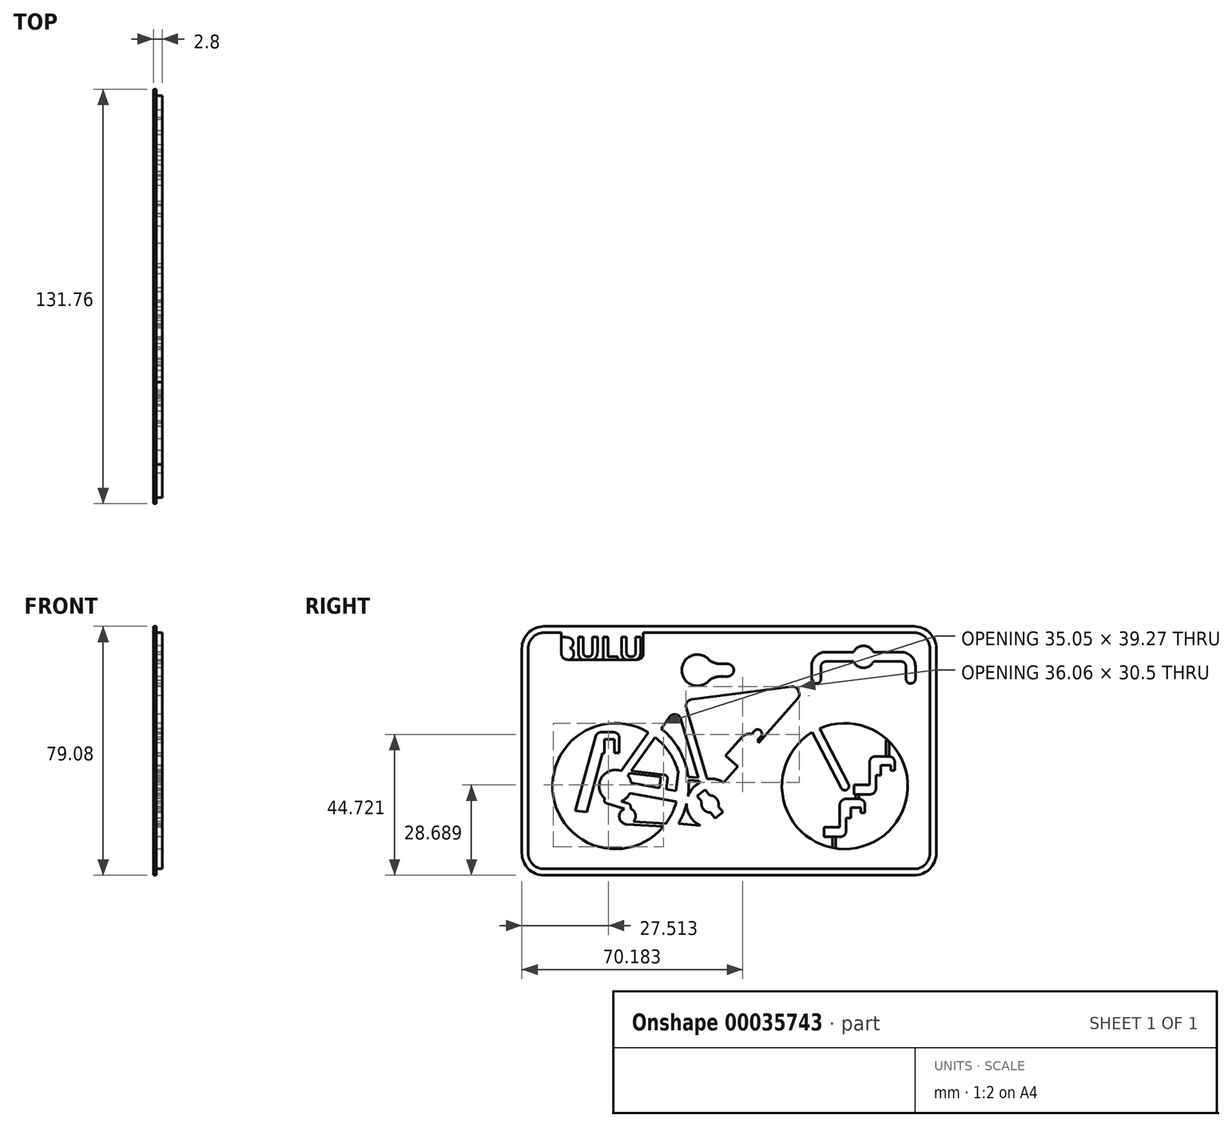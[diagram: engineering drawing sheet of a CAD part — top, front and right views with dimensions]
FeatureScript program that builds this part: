
annotation { "Feature Type Name" : "Feature", "Feature Type Description" : "" }
export const myFeature = defineFeature(function(context is Context, id is Id, definition is map)
    precondition{}
    {
        {
            assignVariable(context, id + "F0", {"name" : "H", "anyValue" : 2.8});
        }
        {
            var Q0;
            Q0=qCreatedBy(makeId("Right.planeOp"),FACE);
            var sketch = newSketch(context, id + "F1", { "sketchPlane" : qUnion([Q0])});
            skArc(sketch, "E0", {"start": v(-24.13, -6.05) * mm, "mid": v(-23.9, -3.4) * mm, "end": v(-23.98, -0.75) * mm});
            skLineSegment(sketch, "E1.0.left", {"start": v(-28.58, 25.85) * mm, "end": v(-32.78, 40.06) * mm});
            skLineSegment(sketch, "E1.0.right", {"start": v(-26.16, 27.08) * mm, "end": v(-30, 40.23) * mm});
            skLineSegment(sketch, "E2.0.startCap", {"start": v(-28.4, 25.23) * mm, "end": v(-28.4, 25.23) * mm});
            skLineSegment(sketch, "E2.0.left", {"start": v(-24.73, 22.24) * mm, "end": v(-18.03, -0.43) * mm});
            skLineSegment(sketch, "E2.0.right", {"start": v(-26.45, 18.66) * mm, "end": v(-20.9, -0.08) * mm});
            skLineSegment(sketch, "E2.1.endCap", {"start": v(-25.84, 25.99) * mm, "end": v(-25.84, 25.99) * mm});
            skLineSegment(sketch, "E2.1.left", {"start": v(-45.44, 2.11) * mm, "end": v(-36.77, 14.32) * mm});
            skLineSegment(sketch, "E2.2.startCap", {"start": v(-28.4, 25.23) * mm, "end": v(-28.4, 25.23) * mm});
            skLineSegment(sketch, "E2.2.endCap", {"start": v(12.78, 30.97) * mm, "end": v(12.78, 30.97) * mm});
            skLineSegment(sketch, "E2.2.left", {"start": v(-26.16, 27.08) * mm, "end": v(9.78, 31.72) * mm});
            skArc(sketch, "E2.3.endCap", {"start": v(14.25, 26) * mm, "mid": v(14.25, 25.99) * mm, "end": v(14.25, 25.98) * mm});
            skLineSegment(sketch, "E2.3.right", {"start": v(-10.81, -3.35) * mm, "end": v(12.38, 22.92) * mm});
            skLineSegment(sketch, "E2.4.left", {"start": v(10.82, 37.6) * mm, "end": v(12.78, 30.97) * mm});
            skLineSegment(sketch, "E2.4.right", {"start": v(8.04, 37.6) * mm, "end": v(9.78, 31.72) * mm});
            skLineSegment(sketch, "E2.5.startCap", {"start": v(10.22, 30.22) * mm, "end": v(10.22, 30.22) * mm});
            skLineSegment(sketch, "E2.5.left", {"start": v(12.78, 30.97) * mm, "end": v(16.41, 18.68) * mm});
            skLineSegment(sketch, "E2.5.right", {"start": v(11.03, 27.5) * mm, "end": v(11.17, 27) * mm});
            skArc(sketch, "E2.6.endCap", {"start": v(26.9, -2.1) * mm, "mid": v(26.33, -3.9) * mm, "end": v(24.53, -3.33) * mm});
            skLineSegment(sketch, "E2.6.left", {"start": v(17.7, 15.6) * mm, "end": v(26.9, -2.1) * mm});
            skLineSegment(sketch, "E2.6.right", {"start": v(15.34, 14.38) * mm, "end": v(24.53, -3.33) * mm});
            skArc(sketch, "E3", {"start": v(15.34, 14.38) * mm, "mid": v(34.93, -20.47) * mm, "end": v(17.7, 15.6) * mm});
            skArc(sketch, "E4", {"start": v(-45.44, 2.11) * mm, "mid": v(-51.68, -0.11) * mm, "end": v(-50.57, -6.64) * mm});
            skLineSegment(sketch, "E5.0.right", {"start": v(-42.59, -4.95) * mm, "end": v(-27.87, -7.72) * mm});
            skLineSegment(sketch, "E6.trimOffspring", {"start": v(-23.07, 24.79) * mm, "end": v(8.85, 28.9) * mm});
            skLineSegment(sketch, "E7.trimOffspring", {"start": v(-43.27, 0.57) * mm, "end": v(-42.74, 1.31) * mm});
            skArc(sketch, "E8.trimOffspring", {"start": v(-42.19, -1.68) * mm, "mid": v(-42.59, -0.49) * mm, "end": v(-43.27, 0.57) * mm});
            skArc(sketch, "E9.trimOffspring", {"start": v(-36.77, 14.32) * mm, "mid": v(-66.97, -5.92) * mm, "end": v(-31.92, -15.58) * mm});
            skArc(sketch, "E10.trimOffspring", {"start": v(-34.83, 17.05) * mm, "mid": v(-70.04, -7.66) * mm, "end": v(-27.76, -15.58) * mm});
            skLineSegment(sketch, "E11.trimOffspring", {"start": v(-32.66, 15.5) * mm, "end": v(-30, 19.25) * mm});
            skLineSegment(sketch, "E12.trimOffspring", {"start": v(-34.83, 17.05) * mm, "end": v(-28.58, 25.85) * mm});
            skLineSegment(sketch, "E13.trimOffspring", {"start": v(-12.8, -1.58) * mm, "end": v(-9.7, 1.94) * mm});
            skLineSegment(sketch, "E14.trimOffspring", {"start": v(12.38, 22.92) * mm, "end": v(14, 17.45) * mm});
            skArc(sketch, "E15.trimOffspring", {"start": v(14, 17.45) * mm, "mid": v(36.24, -23.54) * mm, "end": v(16.41, 18.68) * mm});
            skArc(sketch, "E16", {"start": v(-24.58, -8.33) * mm, "mid": v(-23.45, -12.4) * mm, "end": v(-20.3, -15.22) * mm});
            skLineSegment(sketch, "E17", {"start": v(-43.4, -10.23) * mm, "end": v(-43.4, -10.23) * mm});
            skArc(sketch, "E18.0.endCap", {"start": v(-50.06, -8.17) * mm, "mid": v(-50.7, -7.54) * mm, "end": v(-50.57, -6.64) * mm});
            skArc(sketch, "E18.1.startCap", {"start": v(-50.06, -8.17) * mm, "mid": v(-50.7, -7.54) * mm, "end": v(-50.57, -6.64) * mm});
            skArc(sketch, "E18.1.endCap", {"start": v(-43.1, -8.28) * mm, "mid": v(-42.59, -8.64) * mm, "end": v(-42.4, -9.23) * mm});
            skLineSegment(sketch, "E18.1.right", {"start": v(-50.06, -8.17) * mm, "end": v(-44.44, -9.95) * mm});
            skLineSegment(sketch, "E18.2.left", {"start": v(-42.4, -9.23) * mm, "end": v(-42.4, -9.93) * mm});
            skArc(sketch, "E19.trimOffspring", {"start": v(-45.42, -7.54) * mm, "mid": v(-43.75, -6.52) * mm, "end": v(-42.59, -4.95) * mm});
            skLineSegment(sketch, "E20.trimOffspring", {"start": v(-45.42, -7.54) * mm, "end": v(-43.1, -8.28) * mm});
            skPoint(sketch, "E21.visualSharp", {"position": v(-25.4, 24.49) * mm});
            skArc(sketch, "E21.filletArc", {"start": v(-23.07, 24.79) * mm, "mid": v(-24.49, 23.9) * mm, "end": v(-24.73, 22.24) * mm});
            skPoint(sketch, "E22.visualSharp", {"position": v(-27.62, 22.6) * mm});
            skArc(sketch, "E22.filletArc", {"start": v(-26.45, 18.66) * mm, "mid": v(-28.04, 20.06) * mm, "end": v(-30, 19.25) * mm});
            skPoint(sketch, "E23.visualSharp", {"position": v(10.54, 29.13) * mm});
            skArc(sketch, "E23.filletArc", {"start": v(11.03, 27.5) * mm, "mid": v(10.2, 28.6) * mm, "end": v(8.85, 28.9) * mm});
            skPoint(sketch, "E24.visualSharp", {"position": v(11.49, 25.94) * mm});
            skArc(sketch, "E24.filletArc", {"start": v(10.75, 25.11) * mm, "mid": v(11.2, 26) * mm, "end": v(11.17, 27) * mm});
            skArc(sketch, "E25.trimOffspring", {"start": v(-20.43, -1.7) * mm, "mid": v(-22.71, -3.5) * mm, "end": v(-24.13, -6.05) * mm});
            skArc(sketch, "E26.0.endCap", {"start": v(-6.97, 12.85) * mm, "mid": v(-5.59, 13.74) * mm, "end": v(-3.94, 13.76) * mm});
            skLineSegment(sketch, "E26.0.left", {"start": v(-12.2, 6.92) * mm, "end": v(-6.97, 12.85) * mm});
            skLineSegment(sketch, "E27.trimOffspring", {"start": v(-1.72, 10.98) * mm, "end": v(10.75, 25.11) * mm});
            skLineSegment(sketch, "E28", {"start": v(-12.2, 6.92) * mm, "end": v(-8.33, 3.5) * mm});
            skLineSegment(sketch, "E29", {"start": v(-9.7, 1.94) * mm, "end": v(-8.33, 3.5) * mm});
            skArc(sketch, "E30.0.endCap", {"start": v(-3, 14.84) * mm, "mid": v(-1.11, 14.95) * mm, "end": v(-1, 13.07) * mm});
            skLineSegment(sketch, "E30.0.left", {"start": v(-3.94, 13.76) * mm, "end": v(-3, 14.84) * mm});
            skLineSegment(sketch, "E30.0.right", {"start": v(-1.94, 12) * mm, "end": v(-1, 13.07) * mm});
            skArc(sketch, "E31.trimOffspring", {"start": v(-1.94, 12) * mm, "mid": v(-1.79, 11.5) * mm, "end": v(-1.72, 10.98) * mm});
            skArc(sketch, "E32.0.endCap", {"start": v(-11.57, 36.12) * mm, "mid": v(-9.57, 34.12) * mm, "end": v(-11.57, 32.12) * mm});
            skLineSegment(sketch, "E32.0.left", {"start": v(-13.75, 36.12) * mm, "end": v(-11.57, 36.12) * mm});
            skLineSegment(sketch, "E32.0.right", {"start": v(-13.75, 32.12) * mm, "end": v(-11.57, 32.12) * mm});
            skPoint(sketch, "E33.visualSharp", {"position": v(-17.03, 36.12) * mm});
            skArc(sketch, "E33.filletArc", {"start": v(-17.4, 37.36) * mm, "mid": v(-15.68, 36.44) * mm, "end": v(-13.75, 36.12) * mm});
            skPoint(sketch, "E34.visualSharp", {"position": v(-17.03, 32.12) * mm});
            skArc(sketch, "E34.filletArc", {"start": v(-13.75, 32.12) * mm, "mid": v(-15.68, 31.8) * mm, "end": v(-17.4, 30.88) * mm});
            skLineSegment(sketch, "E35", {"start": v(-32.78, 40.06) * mm, "end": v(-32.78, 43.03) * mm});
            skLineSegment(sketch, "E36", {"start": v(-32.78, 43.03) * mm, "end": v(-30, 43.03) * mm});
            skLineSegment(sketch, "E37", {"start": v(-30, 43.03) * mm, "end": v(-30, 40.23) * mm});
            skLineSegment(sketch, "E38.rect.bottom", {"start": v(-22.8, 35.76) * mm, "end": v(-19.51, 35.76) * mm});
            skLineSegment(sketch, "E38.rect.top", {"start": v(-22.8, 32.47) * mm, "end": v(-19.51, 32.47) * mm});
            skLineSegment(sketch, "E38.rect.left", {"start": v(-22.8, 35.76) * mm, "end": v(-22.8, 32.47) * mm});
            skLineSegment(sketch, "E38.rect.right", {"start": v(-19.51, 35.76) * mm, "end": v(-19.51, 32.47) * mm});
            skPoint(sketch, "E38.rect.middle", {"position": v(-21.16, 34.12) * mm});
            skLineSegment(sketch, "E39", {"start": v(8.04, 37.6) * mm, "end": v(8.04, 40.4) * mm});
            skLineSegment(sketch, "E40", {"start": v(10.82, 37.6) * mm, "end": v(10.82, 40.4) * mm});
            skLineSegment(sketch, "E41", {"start": v(10.82, 40.4) * mm, "end": v(8.04, 40.4) * mm});
            skLineSegment(sketch, "E42.1.startCap", {"start": v(-20.7, -0.1) * mm, "end": v(-20.7, -0.1) * mm});
            skLineSegment(sketch, "E42.1.left", {"start": v(-20.6, -1.12) * mm, "end": v(-23.98, -0.75) * mm});
            skLineSegment(sketch, "E42.1.right", {"start": v(-20.9, -0.08) * mm, "end": v(-24.09, 0.27) * mm});
            skLineSegment(sketch, "E42.2.left", {"start": v(-41.45, -14.01) * mm, "end": v(-31.17, -14.62) * mm});
            skLineSegment(sketch, "E42.2.right", {"start": v(-43.68, -14.88) * mm, "end": v(-31.92, -15.58) * mm});
            skArc(sketch, "E42.3.right", {"start": v(-44.44, -9.95) * mm, "mid": v(-45.92, -12.84) * mm, "end": v(-43.4, -14.9) * mm});
            skArc(sketch, "E42.4.startCap", {"start": v(-17.41, -16.44) * mm, "mid": v(-17.42, -16.43) * mm, "end": v(-17.43, -16.43) * mm});
            skLineSegment(sketch, "E42.4.left", {"start": v(-17.43, -16.43) * mm, "end": v(-27.76, -15.58) * mm});
            skArc(sketch, "E42.5.right", {"start": v(-17.41, -16.44) * mm, "mid": v(-9.88, -12.02) * mm, "end": v(-10.81, -3.35) * mm});
            skArc(sketch, "E42.6.right", {"start": v(-12.8, -1.58) * mm, "mid": v(-15.32, -0.56) * mm, "end": v(-18.03, -0.43) * mm});
            skArc(sketch, "E43.trimOffspring", {"start": v(-24.09, 0.27) * mm, "mid": v(-26.9, 8.72) * mm, "end": v(-32.66, 15.5) * mm});
            skLineSegment(sketch, "E44.trimOffspring", {"start": v(-20.6, -1.12) * mm, "end": v(-20.43, -1.7) * mm});
            skLineSegment(sketch, "E45.trimOffspring", {"start": v(-42.17, 2.12) * mm, "end": v(-34.6, 12.78) * mm});
            skArc(sketch, "E46.trimOffspring", {"start": v(-41.45, -14.01) * mm, "mid": v(-40.88, -11.73) * mm, "end": v(-42.4, -9.93) * mm});
            skArc(sketch, "E47.trimOffspring", {"start": v(-31.17, -14.62) * mm, "mid": v(-29.19, -11.33) * mm, "end": v(-27.87, -7.72) * mm});
            skArc(sketch, "E48.trimOffspring", {"start": v(-27.16, -14.62) * mm, "mid": v(-25.64, -11.57) * mm, "end": v(-24.58, -8.33) * mm});
            skLineSegment(sketch, "E49.trimOffspring", {"start": v(-20.3, -15.22) * mm, "end": v(-27.16, -14.62) * mm});
            skPoint(sketch, "E42.2.endCap.center.orphan", {"position": v(-31.53, -15.1) * mm});
            skPoint(sketch, "E42.4.endCap.center.orphan", {"position": v(-27.45, -15.1) * mm});
            skArc(sketch, "E50.trimOffspring", {"start": v(-17.89, -15.9) * mm, "mid": v(-17.89, -15.9) * mm, "end": v(-17.89, -15.9) * mm});
            skLineSegment(sketch, "E51.rect.bottom", {"start": v(26.14, -12.83) * mm, "end": v(27.64, -12.83) * mm});
            skLineSegment(sketch, "E51.rect.top", {"start": v(26.14, -6.83) * mm, "end": v(30.34, -6.83) * mm});
            skLineSegment(sketch, "E51.rect.right", {"start": v(32.14, -11.23) * mm, "end": v(32.14, -8.62) * mm});
            skPoint(sketch, "E51.rect.middle", {"position": v(29.14, -9.83) * mm});
            skLineSegment(sketch, "E52.0.left", {"start": v(30.84, -9.63) * mm, "end": v(30.84, -11.23) * mm});
            skLineSegment(sketch, "E52.0.right", {"start": v(27.64, -9.63) * mm, "end": v(27.64, -12.83) * mm});
            skPoint(sketch, "E52.0.endCap.center.orphan", {"position": v(29.14, -12.83) * mm});
            skLineSegment(sketch, "E53.rect.top", {"start": v(-51.76, 14.4) * mm, "end": v(-47.77, 14.4) * mm});
            skLineSegment(sketch, "E54.0.left", {"start": v(-47.56, 12.2) * mm, "end": v(-47.56, 7.8) * mm});
            skLineSegment(sketch, "E53.rect.bottom", {"start": v(-51.4, 7.66) * mm, "end": v(-50.76, 7.66) * mm});
            skLineSegment(sketch, "E54.0.right", {"start": v(-50.76, 12.2) * mm, "end": v(-50.76, 7.66) * mm});
            skPoint(sketch, "E53.rect.middle", {"position": v(-48.46, 11.03) * mm});
            skLineSegment(sketch, "E55.bottom", {"start": v(26.14, -6.83) * mm, "end": v(25.93, -6.83) * mm});
            skLineSegment(sketch, "E55.left", {"start": v(26.14, -12.83) * mm, "end": v(26.14, -17.03) * mm});
            skLineSegment(sketch, "E55.right", {"start": v(24.14, -8.62) * mm, "end": v(24.14, -15.83) * mm});
            skLineSegment(sketch, "E56.top", {"start": v(24.14, -15.83) * mm, "end": v(19.14, -15.83) * mm});
            skLineSegment(sketch, "E56.right", {"start": v(19.14, -18.83) * mm, "end": v(19.14, -15.83) * mm});
            skLineSegment(sketch, "E57", {"start": v(19.14, -18.83) * mm, "end": v(24.34, -18.83) * mm});
            skPoint(sketch, "E58.visualSharp", {"position": v(26.14, -18.83) * mm});
            skArc(sketch, "E58.filletArc", {"start": v(24.34, -18.83) * mm, "mid": v(25.6, -18.3) * mm, "end": v(26.14, -17.03) * mm});
            skPoint(sketch, "E59.visualSharp", {"position": v(32.14, -6.83) * mm});
            skArc(sketch, "E59.filletArc", {"start": v(32.14, -8.62) * mm, "mid": v(31.6, -7.35) * mm, "end": v(30.34, -6.83) * mm});
            skPoint(sketch, "E60.visualSharp", {"position": v(24.14, -6.83) * mm});
            skArc(sketch, "E60.filletArc", {"start": v(25.93, -6.83) * mm, "mid": v(24.66, -7.35) * mm, "end": v(24.14, -8.62) * mm});
            skPoint(sketch, "E61.visualSharp", {"position": v(24.14, -15.83) * mm});
            skLineSegment(sketch, "E62", {"start": v(27.64, -9.63) * mm, "end": v(30.84, -9.63) * mm});
            skLineSegment(sketch, "E63", {"start": v(-51.4, 7.66) * mm, "end": v(-56.37, -10.97) * mm});
            skLineSegment(sketch, "E64", {"start": v(-60.02, -10.55) * mm, "end": v(-53.5, 13.08) * mm});
            skPoint(sketch, "E65.visualSharp", {"position": v(-53.13, 14.4) * mm});
            skArc(sketch, "E65.filletArc", {"start": v(-51.76, 14.4) * mm, "mid": v(-52.85, 14.03) * mm, "end": v(-53.5, 13.08) * mm});
            skPoint(sketch, "E66.visualSharp", {"position": v(-45.51, 14.4) * mm});
            skArc(sketch, "E66.filletArc", {"start": v(-45.97, 12.6) * mm, "mid": v(-46.5, 13.87) * mm, "end": v(-47.77, 14.4) * mm});
            skLineSegment(sketch, "E67", {"start": v(-50.76, 12.2) * mm, "end": v(-47.56, 12.2) * mm});
            skLineSegment(sketch, "E68", {"start": v(30.84, -11.23) * mm, "end": v(32.14, -11.23) * mm});
            skPoint(sketch, "E69.trimOffspring.end.orphan", {"position": v(32.14, -12.83) * mm});
            skPoint(sketch, "E70.trimOffspring.end.orphan", {"position": v(41.61, 0.67) * mm});
            skPoint(sketch, "E71.visualSharp", {"position": v(41.61, 6.67) * mm});
            skPoint(sketch, "E72.0.endCap.center.orphan", {"position": v(38.61, 0.67) * mm});
            skPoint(sketch, "E73.rect.middle", {"position": v(38.61, 3.67) * mm});
            skLineSegment(sketch, "E73.rect.top", {"start": v(35.61, 6.67) * mm, "end": v(39.81, 6.67) * mm});
            skPoint(sketch, "E74.visualSharp", {"position": v(35.61, -5.33) * mm});
            skLineSegment(sketch, "E75.left", {"start": v(35.61, 0.67) * mm, "end": v(35.61, -3.53) * mm});
            skPoint(sketch, "E76.visualSharp", {"position": v(33.61, -2.33) * mm});
            skPoint(sketch, "E77.visualSharp", {"position": v(33.61, 6.67) * mm});
            skLineSegment(sketch, "E75.right", {"start": v(33.61, 4.87) * mm, "end": v(33.61, -2.33) * mm});
            skLineSegment(sketch, "E78", {"start": v(28.61, -5.33) * mm, "end": v(33.81, -5.33) * mm});
            skLineSegment(sketch, "E79.top", {"start": v(33.61, -2.33) * mm, "end": v(28.61, -2.33) * mm});
            skLineSegment(sketch, "E73.rect.right", {"start": v(41.61, 2.27) * mm, "end": v(41.61, 4.87) * mm});
            skArc(sketch, "E71.filletArc", {"start": v(41.61, 4.87) * mm, "mid": v(41.09, 6.14) * mm, "end": v(39.81, 6.67) * mm});
            skLineSegment(sketch, "E80", {"start": v(40.31, 2.27) * mm, "end": v(41.61, 2.27) * mm});
            skLineSegment(sketch, "E81", {"start": v(37.11, 3.87) * mm, "end": v(40.31, 3.87) * mm});
            skLineSegment(sketch, "E72.0.right", {"start": v(37.11, 3.87) * mm, "end": v(37.11, 0.67) * mm});
            skLineSegment(sketch, "E73.rect.bottom", {"start": v(35.61, 0.67) * mm, "end": v(37.11, 0.67) * mm});
            skArc(sketch, "E74.filletArc", {"start": v(33.81, -5.33) * mm, "mid": v(35.09, -4.8) * mm, "end": v(35.61, -3.53) * mm});
            skArc(sketch, "E77.filletArc", {"start": v(35.41, 6.67) * mm, "mid": v(34.14, 6.14) * mm, "end": v(33.61, 4.87) * mm});
            skLineSegment(sketch, "E79.right", {"start": v(28.61, -5.33) * mm, "end": v(28.61, -2.33) * mm});
            skLineSegment(sketch, "E72.0.left", {"start": v(40.31, 3.87) * mm, "end": v(40.31, 2.27) * mm});
            skLineSegment(sketch, "E75.bottom", {"start": v(35.61, 6.67) * mm, "end": v(35.41, 6.67) * mm});
            skArc(sketch, "E82.0.endCap", {"start": v(18.16, 31.37) * mm, "mid": v(16.66, 29.87) * mm, "end": v(15.16, 31.37) * mm});
            skArc(sketch, "E82.5.endCap", {"start": v(48.16, 31.37) * mm, "mid": v(46.66, 29.87) * mm, "end": v(45.16, 31.37) * mm});
            skLineSegment(sketch, "E82.0.right", {"start": v(15.16, 35.37) * mm, "end": v(15.16, 31.37) * mm});
            skLineSegment(sketch, "E82.0.left", {"start": v(18.16, 35.37) * mm, "end": v(18.16, 31.37) * mm});
            skLineSegment(sketch, "E82.5.right", {"start": v(45.16, 35.37) * mm, "end": v(45.16, 31.37) * mm});
            skLineSegment(sketch, "E82.5.left", {"start": v(48.16, 35.37) * mm, "end": v(48.16, 31.37) * mm});
            skArc(sketch, "E83", {"start": v(28.5, 36.87) * mm, "mid": v(31.66, 34.87) * mm, "end": v(34.83, 36.87) * mm});
            skArc(sketch, "E82.1.right", {"start": v(19.66, 39.87) * mm, "mid": v(16.48, 38.55) * mm, "end": v(15.16, 35.37) * mm});
            skArc(sketch, "E82.1.left", {"start": v(19.66, 36.87) * mm, "mid": v(18.6, 36.43) * mm, "end": v(18.16, 35.37) * mm});
            skLineSegment(sketch, "E84.trimOffspring", {"start": v(28.5, 36.87) * mm, "end": v(19.66, 36.87) * mm});
            skLineSegment(sketch, "E85.trimOffspring", {"start": v(34.83, 36.87) * mm, "end": v(43.66, 36.87) * mm});
            skArc(sketch, "E82.4.left", {"start": v(45.16, 35.37) * mm, "mid": v(44.72, 36.43) * mm, "end": v(43.66, 36.87) * mm});
            skArc(sketch, "E82.4.right", {"start": v(48.16, 35.37) * mm, "mid": v(46.84, 38.55) * mm, "end": v(43.66, 39.87) * mm});
            skPoint(sketch, "E86.visualSharp", {"position": v(16.66, 38.37) * mm});
            skPoint(sketch, "E87.visualSharp", {"position": v(46.66, 38.37) * mm});
            skLineSegment(sketch, "E88.trimOffspring", {"start": v(28.5, 39.87) * mm, "end": v(19.66, 39.87) * mm});
            skLineSegment(sketch, "E89.trimOffspring", {"start": v(34.83, 39.87) * mm, "end": v(43.66, 39.87) * mm});
            skArc(sketch, "E90.trimOffspring", {"start": v(34.83, 39.87) * mm, "mid": v(31.66, 41.87) * mm, "end": v(28.5, 39.87) * mm});
            skLineSegment(sketch, "E91.bottom", {"start": v(-69.96, -29.05) * mm, "end": v(47.8, -29.05) * mm});
            skLineSegment(sketch, "E91.top", {"start": v(-69.96, 46.03) * mm, "end": v(47.8, 46.03) * mm});
            skLineSegment(sketch, "E91.left", {"start": v(-74.96, -24.05) * mm, "end": v(-74.96, 41.03) * mm});
            skLineSegment(sketch, "E91.right", {"start": v(52.8, -24.05) * mm, "end": v(52.8, 41.03) * mm});
            skPoint(sketch, "E92.visualSharp", {"position": v(-74.96, 46.03) * mm});
            skArc(sketch, "E92.filletArc", {"start": v(-69.96, 46.03) * mm, "mid": v(-73.5, 44.56) * mm, "end": v(-74.96, 41.03) * mm});
            skPoint(sketch, "E93.visualSharp", {"position": v(-74.96, -29.05) * mm});
            skArc(sketch, "E93.filletArc", {"start": v(-74.96, -24.05) * mm, "mid": v(-73.5, -27.58) * mm, "end": v(-69.96, -29.05) * mm});
            skPoint(sketch, "E94.visualSharp", {"position": v(52.8, 46.03) * mm});
            skArc(sketch, "E94.filletArc", {"start": v(52.8, 41.03) * mm, "mid": v(51.33, 44.56) * mm, "end": v(47.8, 46.03) * mm});
            skPoint(sketch, "E95.visualSharp", {"position": v(52.8, -29.05) * mm});
            skArc(sketch, "E95.filletArc", {"start": v(47.8, -29.05) * mm, "mid": v(51.33, -27.58) * mm, "end": v(52.8, -24.05) * mm});
            skArc(sketch, "E96", {"start": v(-17.4, 37.36) * mm, "mid": v(-26.11, 34.12) * mm, "end": v(-17.4, 30.88) * mm});
            skLineSegment(sketch, "E97", {"start": v(-47.56, 7.8) * mm, "end": v(-45.97, 7.8) * mm});
            skPoint(sketch, "E98.orphan", {"position": v(-47.56, 3.4) * mm});
            skLineSegment(sketch, "E99", {"start": v(-45.97, 12.6) * mm, "end": v(-45.97, 7.8) * mm});
            skLineSegment(sketch, "E100.bottom", {"start": v(-64.46, 46.03) * mm, "end": v(-38.35, 46.03) * mm});
            skLineSegment(sketch, "E100.top", {"start": v(-62.46, 37.48) * mm, "end": v(-40.35, 37.48) * mm});
            skLineSegment(sketch, "E100.left", {"start": v(-64.46, 46.03) * mm, "end": v(-64.46, 39.48) * mm});
            skLineSegment(sketch, "E100.right", {"start": v(-38.35, 46.03) * mm, "end": v(-38.35, 39.48) * mm});
            skText(sketch, "E101", { "text": "BULU", "fontName": "OpenSans-Bold.ttf"});
            skPoint(sketch, "E102.visualSharp", {"position": v(-38.35, 37.48) * mm});
            skArc(sketch, "E102.filletArc", {"start": v(-40.35, 37.48) * mm, "mid": v(-38.93, 38.06) * mm, "end": v(-38.35, 39.48) * mm});
            skPoint(sketch, "E103.visualSharp", {"position": v(-64.46, 37.48) * mm});
            skArc(sketch, "E103.filletArc", {"start": v(-64.46, 39.48) * mm, "mid": v(-63.87, 38.06) * mm, "end": v(-62.46, 37.48) * mm});
            skLineSegment(sketch, "E104.trimOffspring", {"start": v(-31.7, 0.85) * mm, "end": v(-42.17, 2.12) * mm});
            skLineSegment(sketch, "E105.0", {"start": v(-16.97, -11.15) * mm, "end": v(-15.5, -12.96) * mm});
            skArc(sketch, "E105.1", {"start": v(-19.77, -7.69) * mm, "mid": v(-19.22, -10.1) * mm, "end": v(-16.97, -11.15) * mm});
            skLineSegment(sketch, "E105.2", {"start": v(-19.77, -7.69) * mm, "end": v(-21.2, -5.92) * mm});
            skLineSegment(sketch, "E105.3", {"start": v(-21.2, -5.92) * mm, "end": v(-18.71, -3.9) * mm});
            skLineSegment(sketch, "E105.4", {"start": v(-17.28, -5.68) * mm, "end": v(-18.71, -3.9) * mm});
            skLineSegment(sketch, "E105.5", {"start": v(-15.5, -12.96) * mm, "end": v(-13.02, -10.95) * mm});
            skArc(sketch, "E105.6", {"start": v(-14.48, -9.14) * mm, "mid": v(-15.03, -6.72) * mm, "end": v(-17.28, -5.68) * mm});
            skLineSegment(sketch, "E105.7", {"start": v(-14.48, -9.14) * mm, "end": v(-13.02, -10.95) * mm});
            skLineSegment(sketch, "E106.0", {"start": v(30.02, 40) * mm, "end": v(33.22, 40) * mm});
            skLineSegment(sketch, "E106.1", {"start": v(30.02, 40) * mm, "end": v(30.02, 36.72) * mm});
            skLineSegment(sketch, "E106.2", {"start": v(30.02, 36.72) * mm, "end": v(33.22, 36.72) * mm});
            skLineSegment(sketch, "E106.3", {"start": v(33.22, 40) * mm, "end": v(33.22, 36.72) * mm});
            skLineSegment(sketch, "E107.0", {"start": v(-69.96, -31.05) * mm, "end": v(47.8, -31.05) * mm});
            skArc(sketch, "E107.1", {"start": v(-76.96, -24.05) * mm, "mid": v(-74.91, -29) * mm, "end": v(-69.96, -31.05) * mm});
            skLineSegment(sketch, "E107.2", {"start": v(-76.96, -24.05) * mm, "end": v(-76.96, 41.03) * mm});
            skArc(sketch, "E107.3", {"start": v(-69.96, 48.03) * mm, "mid": v(-74.91, 45.98) * mm, "end": v(-76.96, 41.03) * mm});
            skLineSegment(sketch, "E107.4", {"start": v(-69.96, 48.03) * mm, "end": v(47.8, 48.03) * mm});
            skArc(sketch, "E107.5", {"start": v(47.8, -31.05) * mm, "mid": v(52.75, -29) * mm, "end": v(54.8, -24.05) * mm});
            skArc(sketch, "E107.6", {"start": v(54.8, 41.03) * mm, "mid": v(52.75, 45.98) * mm, "end": v(47.8, 48.03) * mm});
            skLineSegment(sketch, "E107.7", {"start": v(54.8, -24.05) * mm, "end": v(54.8, 41.03) * mm});
            skPoint(sketch, "E108.end.orphan", {"position": v(-52.92, 14.4) * mm});
            skPoint(sketch, "E109.visualSharp", {"position": v(-30.15, 0.66) * mm});
            skArc(sketch, "E110.trimOffspring", {"start": v(-27.3, 1.71) * mm, "mid": v(-30, 7.87) * mm, "end": v(-34.6, 12.78) * mm});
            skLineSegment(sketch, "E111", {"start": v(-28.01, -4.26) * mm, "end": v(-31.04, -3.7) * mm});
            skLineSegment(sketch, "E112", {"start": v(-28.01, -4.26) * mm, "end": v(-27.3, 1.71) * mm});
            skLineSegment(sketch, "E113", {"start": v(-31.04, -3.7) * mm, "end": v(-30.65, -0.48) * mm});
            skLineSegment(sketch, "E114.trimOffspring", {"start": v(-32.75, 0.22) * mm, "end": v(-42.74, 1.31) * mm});
            skLineSegment(sketch, "E115", {"start": v(-33.18, -3.32) * mm, "end": v(-32.75, 0.22) * mm});
            skPoint(sketch, "E116.visualSharp", {"position": v(-30.51, 0.7) * mm});
            skArc(sketch, "E116.filletArc", {"start": v(-30.65, -0.48) * mm, "mid": v(-30.9, 0.4) * mm, "end": v(-31.7, 0.85) * mm});
            skLineSegment(sketch, "E117", {"start": v(-60.02, -10.55) * mm, "end": v(-56.37, -10.97) * mm});
            skLineSegment(sketch, "E118.trimOffspring", {"start": v(-33.18, -3.32) * mm, "end": v(-42.19, -1.68) * mm});
            const initialGuessF1  = {"E101": [-0.06296, 0.03873, 1, 0, 0.0062]};
            skSetInitialGuess(sketch, initialGuessF1);
            skSolve(sketch);
        }
        {
            var Q0;
            Q0=makeQuery(id+"F1.imprint","IMPRINT",FACE,{"disambiguationData":[TD([[makeQuery(id+"F1.imprint","IMPRINT",EDGE,{"derivedFrom":sQuery(id+"F1.wireOp",EDGE,"d670718d-e32d-4bfd-a30b-cf72b9636345")}),1.0]])]});
            var Q1;
            Q1=makeQuery(id+"F1.imprint","IMPRINT",FACE,{"disambiguationData":[TD([[makeQuery(id+"F1.imprint","IMPRINT",EDGE,{"derivedFrom":sQuery(id+"F1.wireOp",EDGE,"4c950c17-0d4c-4f3a-b05d-0eab68311945")}),1.0]])]});
            var Q2;
            Q2=makeQuery(id+"F1.imprint","IMPRINT",FACE,{"disambiguationData":[TD([[makeQuery(id+"F1.imprint","IMPRINT",EDGE,{"derivedFrom":sQuery(id+"F1.wireOp",EDGE,"E0")}),1.0]])]});
            var Q3;
            Q3=makeQuery(id+"F1.imprint","IMPRINT",FACE,{"disambiguationData":[TD([[makeQuery(id+"F1.imprint","IMPRINT",EDGE,{"derivedFrom":sQuery(id+"F1.wireOp",EDGE,"feb6c065-ad3e-4e5b-ba5c-cb6fa5ef12440.MirrorCS")}),-1.0]])]});
            var Q4;
            Q4=makeQuery(id+"F1.imprint","IMPRINT",FACE,{"disambiguationData":[TD([[makeQuery(id+"F1.imprint","IMPRINT",EDGE,{"derivedFrom":sQuery(id+"F1.wireOp",EDGE,"E53.rect.left")}),-1.0]])]});
            var Q5;
            Q5=makeQuery(id+"F1.imprint","IMPRINT",FACE,{"disambiguationData":[TD([[makeQuery(id+"F1.imprint","IMPRINT",EDGE,{"derivedFrom":sQuery(id+"F1.wireOp",EDGE,"E51.rect.bottom")}),1.0]])]});
            var Q6;
            Q6=makeQuery(id+"F1.imprint","IMPRINT",FACE,{"disambiguationData":[TD([[makeQuery(id+"F1.imprint","IMPRINT",EDGE,{"derivedFrom":sQuery(id+"F1.wireOp",EDGE,"6e1ddf8b-da26-4d41-9c80-b6f64bdec91b.rect.right")}),1.0]])]});
            var Q7;
            Q7=makeQuery(id+"F1.imprint","IMPRINT",FACE,{"disambiguationData":[TD([[makeQuery(id+"F1.imprint","IMPRINT",EDGE,{"derivedFrom":sQuery(id+"F1.wireOp",EDGE,"E54.0.startCap")}),1.0]])]});
            var Q8;
            Q8=makeQuery(id+"F1.imprint","IMPRINT",FACE,{"disambiguationData":[TD([[makeQuery(id+"F1.imprint","IMPRINT",EDGE,{"derivedFrom":sQuery(id+"F1.wireOp",EDGE,"E53.rect.top")}),-1.0]])]});
            var Q9;
            Q9=makeQuery(id+"F1.imprint","IMPRINT",FACE,{"disambiguationData":[TD([[makeQuery(id+"F1.imprint","IMPRINT",EDGE,{"derivedFrom":sQuery(id+"F1.wireOp",EDGE,"E32.0.endCap")}),-1.0]])]});
            var Q10;
            Q10=makeQuery(id+"F1.imprint","IMPRINT",FACE,{"disambiguationData":[TD([[makeQuery(id+"F1.imprint","IMPRINT",EDGE,{"derivedFrom":sQuery(id+"F1.wireOp",EDGE,"E82.0.endCap")}),-1.0]])]});
            var Q11;
            Q11=makeQuery(id+"F1.imprint","IMPRINT",FACE,{"disambiguationData":[TD([[makeQuery(id+"F1.imprint","IMPRINT",EDGE,{"derivedFrom":sQuery(id+"F1.wireOp",EDGE,"E73.rect.top")}),-1.0]])]});
            extrude(context, id + "F2", {"entities" : qUnion([Q0, Q1, Q2, Q3, Q4, Q5, Q6, Q7, Q8, Q9, Q10, Q11]), "depth" : (getVariable(context, 'H')) * mm});
        }
        {
            var Q0;
            Q0=makeQuery(id+"F1.imprint","IMPRINT",FACE,{"disambiguationData":[TD([[makeQuery(id+"F1.imprint","IMPRINT",EDGE,{"derivedFrom":sQuery(id+"F1.wireOp",EDGE,"E91.bottom")}),-1.0]])]});
            var Q1;
            {var subQ0=sQuery(id+"F2vLRuSNgIglzrC_7.wireOp",EDGE,"440b115a-4ba2-4160-832b-be8f7d272a83");Q1=makeQuery(id+"F5863CYNAVBMcLV_21.opThicken","SWEPT_FACE",FACE,{"disambiguationData":[OSD([subQ0]),TDD([makeQuery(id+"F2ZETnk0Khb3zFe_7.opExtrude","CAP_EDGE",EDGE,{"disambiguationData":[OSD([subQ0])],"isStart":false})])]});}
            extrude(context, id + "F3", {"entities" : qUnion([Q0]), "endBoundEntityFace" : qUnion([Q1]), "depth" : (getVariable(context, 'H') / 3) * mm});
        }
        {
            var Q0;
            Q0=qCreatedBy(makeId("Right.planeOp"),FACE);
            var sketch = newSketch(context, id + "F4", { "sketchPlane" : qUnion([Q0])});
            skLineSegment(sketch, "E119", {"start": v(-70.52, -2.5) * mm, "end": v(-70.92, -2.5) * mm});
            skLineSegment(sketch, "E120", {"start": v(-70.92, -2.5) * mm, "end": v(-74.96, -2.5) * mm});
            skArc(sketch, "E121.0.startCap", {"start": v(-70.92, -2) * mm, "mid": v(-70.42, -2.5) * mm, "end": v(-70.92, -3) * mm});
            skArc(sketch, "E121.0.endCap", {"start": v(-74.96, -3) * mm, "mid": v(-75.46, -2.5) * mm, "end": v(-74.96, -2) * mm});
            skLineSegment(sketch, "E121.0.left", {"start": v(-70.92, -3) * mm, "end": v(-74.96, -3) * mm});
            skLineSegment(sketch, "E121.0.right", {"start": v(-70.92, -2) * mm, "end": v(-74.96, -2) * mm});
            skLineSegment(sketch, "E122", {"start": v(-66.82, -2.5) * mm, "end": v(-58.15, -2.5) * mm});
            skArc(sketch, "E123.0.startCap", {"start": v(-66.82, -3) * mm, "mid": v(-67.32, -2.5) * mm, "end": v(-66.82, -2) * mm});
            skArc(sketch, "E123.0.endCap", {"start": v(-58.15, -2) * mm, "mid": v(-57.65, -2.5) * mm, "end": v(-58.15, -3) * mm});
            skLineSegment(sketch, "E123.0.left", {"start": v(-66.82, -2) * mm, "end": v(-58.15, -2) * mm});
            skLineSegment(sketch, "E123.0.right", {"start": v(-66.82, -3) * mm, "end": v(-58.15, -3) * mm});
            skLineSegment(sketch, "E124", {"start": v(-49.24, 14.04) * mm, "end": v(-49.24, 16.76) * mm});
            skArc(sketch, "E125.0.startCap", {"start": v(-48.74, 14.04) * mm, "mid": v(-49.24, 13.54) * mm, "end": v(-49.74, 14.04) * mm});
            skArc(sketch, "E125.0.endCap", {"start": v(-49.74, 16.76) * mm, "mid": v(-49.24, 17.26) * mm, "end": v(-48.74, 16.76) * mm});
            skLineSegment(sketch, "E125.0.left", {"start": v(-49.74, 14.04) * mm, "end": v(-49.74, 16.76) * mm});
            skLineSegment(sketch, "E125.0.right", {"start": v(-48.74, 14.04) * mm, "end": v(-48.74, 16.76) * mm});
            skLineSegment(sketch, "E126", {"start": v(-31.46, 43.36) * mm, "end": v(-31.46, 46.46) * mm});
            skArc(sketch, "E127.0.startCap", {"start": v(-30.96, 43.36) * mm, "mid": v(-31.46, 42.86) * mm, "end": v(-31.96, 43.36) * mm});
            skArc(sketch, "E127.0.endCap", {"start": v(-31.96, 46.46) * mm, "mid": v(-31.46, 46.96) * mm, "end": v(-30.96, 46.46) * mm});
            skLineSegment(sketch, "E127.0.left", {"start": v(-31.96, 43.36) * mm, "end": v(-31.96, 46.46) * mm});
            skLineSegment(sketch, "E127.0.right", {"start": v(-30.96, 43.36) * mm, "end": v(-30.96, 46.46) * mm});
            skLineSegment(sketch, "E128.0.left", {"start": v(-13.85, 29.1) * mm, "end": v(-13.85, 31.68) * mm});
            skLineSegment(sketch, "E129", {"start": v(-13.35, 29.1) * mm, "end": v(-13.35, 31.68) * mm});
            skLineSegment(sketch, "E128.0.right", {"start": v(-12.85, 29.1) * mm, "end": v(-12.85, 31.68) * mm});
            skArc(sketch, "E128.0.endCap", {"start": v(-13.85, 31.68) * mm, "mid": v(-13.35, 32.18) * mm, "end": v(-12.85, 31.68) * mm});
            skArc(sketch, "E128.0.startCap", {"start": v(-12.85, 29.1) * mm, "mid": v(-13.35, 28.6) * mm, "end": v(-13.85, 29.1) * mm});
            skLineSegment(sketch, "E130.0.left", {"start": v(31.09, 42.17) * mm, "end": v(31.09, 46.38) * mm});
            skLineSegment(sketch, "E131", {"start": v(31.59, 42.17) * mm, "end": v(31.59, 46.38) * mm});
            skLineSegment(sketch, "E130.0.right", {"start": v(32.09, 42.17) * mm, "end": v(32.09, 46.38) * mm});
            skArc(sketch, "E130.0.endCap", {"start": v(31.09, 46.38) * mm, "mid": v(31.59, 46.88) * mm, "end": v(32.09, 46.38) * mm});
            skArc(sketch, "E130.0.startCap", {"start": v(32.09, 42.17) * mm, "mid": v(31.59, 41.67) * mm, "end": v(31.09, 42.17) * mm});
            skLineSegment(sketch, "E132.0.left", {"start": v(21.8, -22.07) * mm, "end": v(21.8, -19.2) * mm});
            skLineSegment(sketch, "E133", {"start": v(22.3, -22.07) * mm, "end": v(22.3, -19.2) * mm});
            skLineSegment(sketch, "E132.0.right", {"start": v(22.8, -22.07) * mm, "end": v(22.8, -19.2) * mm});
            skArc(sketch, "E132.0.endCap", {"start": v(21.8, -19.2) * mm, "mid": v(22.3, -18.7) * mm, "end": v(22.8, -19.2) * mm});
            skArc(sketch, "E132.0.startCap", {"start": v(22.8, -22.07) * mm, "mid": v(22.3, -22.57) * mm, "end": v(21.8, -22.07) * mm});
            skLineSegment(sketch, "E134.0.left", {"start": v(29.16, -6.42) * mm, "end": v(29.16, -5.63) * mm});
            skLineSegment(sketch, "E135", {"start": v(29.66, -6.42) * mm, "end": v(29.66, -5.63) * mm});
            skLineSegment(sketch, "E134.0.right", {"start": v(30.16, -6.42) * mm, "end": v(30.16, -5.63) * mm});
            skArc(sketch, "E134.0.endCap", {"start": v(29.16, -5.63) * mm, "mid": v(29.66, -5.13) * mm, "end": v(30.16, -5.63) * mm});
            skArc(sketch, "E134.0.startCap", {"start": v(30.16, -6.42) * mm, "mid": v(29.66, -6.92) * mm, "end": v(29.16, -6.42) * mm});
            skLineSegment(sketch, "E136.0.left", {"start": v(38.8, 6.98) * mm, "end": v(38.8, 11.46) * mm});
            skLineSegment(sketch, "E137", {"start": v(39.3, 6.98) * mm, "end": v(39.3, 11.46) * mm});
            skLineSegment(sketch, "E136.0.right", {"start": v(39.8, 6.98) * mm, "end": v(39.8, 11.46) * mm});
            skArc(sketch, "E136.0.endCap", {"start": v(38.8, 11.46) * mm, "mid": v(39.3, 11.96) * mm, "end": v(39.8, 11.46) * mm});
            skArc(sketch, "E136.0.startCap", {"start": v(39.8, 6.98) * mm, "mid": v(39.3, 6.48) * mm, "end": v(38.8, 6.98) * mm});
            skLineSegment(sketch, "E138.0.left", {"start": v(53.16, -3.94) * mm, "end": v(49.26, -3.94) * mm});
            skLineSegment(sketch, "E139", {"start": v(53.16, -3.44) * mm, "end": v(49.26, -3.44) * mm});
            skLineSegment(sketch, "E138.0.right", {"start": v(53.16, -2.94) * mm, "end": v(49.26, -2.94) * mm});
            skArc(sketch, "E138.0.endCap", {"start": v(49.26, -3.94) * mm, "mid": v(48.76, -3.44) * mm, "end": v(49.26, -2.94) * mm});
            skArc(sketch, "E138.0.startCap", {"start": v(53.16, -2.94) * mm, "mid": v(53.66, -3.44) * mm, "end": v(53.16, -3.94) * mm});
            skArc(sketch, "E140.0.endCap", {"start": v(11.94, 33.97) * mm, "mid": v(11.44, 34.47) * mm, "end": v(11.94, 34.97) * mm});
            skLineSegment(sketch, "E140.0.left", {"start": v(14.88, 33.97) * mm, "end": v(11.94, 33.97) * mm});
            skArc(sketch, "E140.0.startCap", {"start": v(14.88, 34.97) * mm, "mid": v(15.38, 34.47) * mm, "end": v(14.88, 33.97) * mm});
            skLineSegment(sketch, "E141", {"start": v(14.88, 34.47) * mm, "end": v(11.94, 34.47) * mm});
            skLineSegment(sketch, "E140.0.right", {"start": v(14.88, 34.97) * mm, "end": v(11.94, 34.97) * mm});
            skArc(sketch, "E142.0.endCap", {"start": v(48.46, 33.4) * mm, "mid": v(47.96, 33.9) * mm, "end": v(48.46, 34.4) * mm});
            skLineSegment(sketch, "E142.0.left", {"start": v(52.97, 33.4) * mm, "end": v(48.46, 33.4) * mm});
            skArc(sketch, "E142.0.startCap", {"start": v(52.97, 34.4) * mm, "mid": v(53.47, 33.9) * mm, "end": v(52.97, 33.4) * mm});
            skLineSegment(sketch, "E143", {"start": v(52.97, 33.9) * mm, "end": v(48.46, 33.9) * mm});
            skLineSegment(sketch, "E142.0.right", {"start": v(52.97, 34.4) * mm, "end": v(48.46, 34.4) * mm});
            skArc(sketch, "E144.0.endCap", {"start": v(-27.9, 33.62) * mm, "mid": v(-28.4, 34.12) * mm, "end": v(-27.9, 34.62) * mm});
            skLineSegment(sketch, "E144.0.left", {"start": v(-26.5, 33.62) * mm, "end": v(-27.9, 33.62) * mm});
            skArc(sketch, "E144.0.startCap", {"start": v(-26.5, 34.62) * mm, "mid": v(-26, 34.12) * mm, "end": v(-26.5, 33.62) * mm});
            skLineSegment(sketch, "E145", {"start": v(-26.5, 34.12) * mm, "end": v(-27.9, 34.12) * mm});
            skLineSegment(sketch, "E144.0.right", {"start": v(-26.5, 34.62) * mm, "end": v(-27.9, 34.62) * mm});
            skLineSegment(sketch, "E146.0.left", {"start": v(25.1, -29.2) * mm, "end": v(25.1, -26.33) * mm});
            skLineSegment(sketch, "E147", {"start": v(25.6, -29.2) * mm, "end": v(25.6, -26.33) * mm});
            skLineSegment(sketch, "E146.0.right", {"start": v(26.1, -29.2) * mm, "end": v(26.1, -26.33) * mm});
            skArc(sketch, "E146.0.startCap", {"start": v(26.1, -29.2) * mm, "mid": v(25.6, -29.7) * mm, "end": v(25.1, -29.2) * mm});
            skArc(sketch, "E146.0.endCap", {"start": v(25.1, -26.33) * mm, "mid": v(25.6, -25.83) * mm, "end": v(26.1, -26.33) * mm});
            skLineSegment(sketch, "E148.0.left", {"start": v(-47.87, -29.22) * mm, "end": v(-47.87, -26.35) * mm});
            skLineSegment(sketch, "E149", {"start": v(-47.37, -29.22) * mm, "end": v(-47.37, -26.35) * mm});
            skLineSegment(sketch, "E148.0.right", {"start": v(-46.87, -29.22) * mm, "end": v(-46.87, -26.35) * mm});
            skArc(sketch, "E148.0.startCap", {"start": v(-46.87, -29.22) * mm, "mid": v(-47.37, -29.72) * mm, "end": v(-47.87, -29.22) * mm});
            skArc(sketch, "E148.0.endCap", {"start": v(-47.87, -26.35) * mm, "mid": v(-47.37, -25.85) * mm, "end": v(-46.87, -26.35) * mm});
            skLineSegment(sketch, "E150.0.left", {"start": v(8.85, 40.67) * mm, "end": v(8.85, 46.06) * mm});
            skLineSegment(sketch, "E151", {"start": v(9.35, 40.67) * mm, "end": v(9.35, 46.06) * mm});
            skLineSegment(sketch, "E150.0.right", {"start": v(9.85, 40.67) * mm, "end": v(9.85, 46.06) * mm});
            skArc(sketch, "E150.0.startCap", {"start": v(9.85, 40.67) * mm, "mid": v(9.35, 40.17) * mm, "end": v(8.85, 40.67) * mm});
            skArc(sketch, "E150.0.endCap", {"start": v(8.85, 46.06) * mm, "mid": v(9.35, 46.56) * mm, "end": v(9.85, 46.06) * mm});
            skSolve(sketch);
        }
        {
            var Q0;
            Q0=makeQuery(id+"F4.imprint","IMPRINT",FACE,{"disambiguationData":[TD([[makeQuery(id+"F4.imprint","IMPRINT",EDGE,{"derivedFrom":sQuery(id+"F4.wireOp",EDGE,"E125.0.startCap")}),-1.0]])]});
            var Q1;
            Q1=makeQuery(id+"F4.imprint","IMPRINT",FACE,{"disambiguationData":[TD([[makeQuery(id+"F4.imprint","IMPRINT",EDGE,{"derivedFrom":sQuery(id+"F4.wireOp",EDGE,"E123.0.startCap")}),-1.0]])]});
            var Q2;
            Q2=makeQuery(id+"F4.imprint","IMPRINT",FACE,{"disambiguationData":[TD([[makeQuery(id+"F4.imprint","IMPRINT",EDGE,{"derivedFrom":sQuery(id+"F4.wireOp",EDGE,"E121.0.startCap")}),-1.0]])]});
            var Q3;
            Q3=makeQuery(id+"F4.imprint","IMPRINT",FACE,{"disambiguationData":[TD([[makeQuery(id+"F4.imprint","IMPRINT",EDGE,{"derivedFrom":sQuery(id+"F4.wireOp",EDGE,"E127.0.startCap")}),-1.0]])]});
            var Q4;
            Q4=makeQuery(id+"F4.imprint","IMPRINT",FACE,{"disambiguationData":[TD([[makeQuery(id+"F4.imprint","IMPRINT",EDGE,{"derivedFrom":sQuery(id+"F4.wireOp",EDGE,"E144.0.endCap")}),-1.0]])]});
            var Q5;
            Q5=makeQuery(id+"F4.imprint","IMPRINT",FACE,{"disambiguationData":[TD([[makeQuery(id+"F4.imprint","IMPRINT",EDGE,{"derivedFrom":sQuery(id+"F4.wireOp",EDGE,"E128.0.left")}),-1.0]])]});
            var Q6;
            Q6=makeQuery(id+"F4.imprint","IMPRINT",FACE,{"disambiguationData":[TD([[makeQuery(id+"F4.imprint","IMPRINT",EDGE,{"derivedFrom":sQuery(id+"F4.wireOp",EDGE,"E150.0.left")}),-1.0]])]});
            var Q7;
            Q7=makeQuery(id+"F4.imprint","IMPRINT",FACE,{"disambiguationData":[TD([[makeQuery(id+"F4.imprint","IMPRINT",EDGE,{"derivedFrom":sQuery(id+"F4.wireOp",EDGE,"E140.0.endCap")}),-1.0]])]});
            var Q8;
            Q8=makeQuery(id+"F4.imprint","IMPRINT",FACE,{"disambiguationData":[TD([[makeQuery(id+"F4.imprint","IMPRINT",EDGE,{"derivedFrom":sQuery(id+"F4.wireOp",EDGE,"E142.0.endCap")}),-1.0]])]});
            var Q9;
            Q9=makeQuery(id+"F4.imprint","IMPRINT",FACE,{"disambiguationData":[TD([[makeQuery(id+"F4.imprint","IMPRINT",EDGE,{"derivedFrom":sQuery(id+"F4.wireOp",EDGE,"E136.0.left")}),-1.0]])]});
            var Q10;
            Q10=makeQuery(id+"F4.imprint","IMPRINT",FACE,{"disambiguationData":[TD([[makeQuery(id+"F4.imprint","IMPRINT",EDGE,{"derivedFrom":sQuery(id+"F4.wireOp",EDGE,"E138.0.left")}),-1.0]])]});
            var Q11;
            Q11=makeQuery(id+"F4.imprint","IMPRINT",FACE,{"disambiguationData":[TD([[makeQuery(id+"F4.imprint","IMPRINT",EDGE,{"derivedFrom":sQuery(id+"F4.wireOp",EDGE,"E134.0.left")}),-1.0]])]});
            var Q12;
            Q12=makeQuery(id+"F4.imprint","IMPRINT",FACE,{"disambiguationData":[TD([[makeQuery(id+"F4.imprint","IMPRINT",EDGE,{"derivedFrom":sQuery(id+"F4.wireOp",EDGE,"E132.0.left")}),-1.0]])]});
            var Q13;
            Q13=makeQuery(id+"F4.imprint","IMPRINT",FACE,{"disambiguationData":[TD([[makeQuery(id+"F4.imprint","IMPRINT",EDGE,{"derivedFrom":sQuery(id+"F4.wireOp",EDGE,"E146.0.left")}),-1.0]])]});
            var Q14;
            Q14=makeQuery(id+"F4.imprint","IMPRINT",FACE,{"disambiguationData":[TD([[makeQuery(id+"F4.imprint","IMPRINT",EDGE,{"derivedFrom":sQuery(id+"F4.wireOp",EDGE,"E148.0.left")}),-1.0]])]});
            extrude(context, id + "F5", {"entities" : qUnion([Q0, Q1, Q2, Q3, Q4, Q5, Q6, Q7, Q8, Q9, Q10, Q11, Q12, Q13, Q14]), "operationType" : NewBodyOperationType.ADD, "depth" : (getVariable(context, 'H') / 3) * mm});
        }
        {
            var Q0;
            Q0=qCreatedBy(makeId("Right.planeOp"),FACE);
            var sketch = newSketch(context, id + "F6", { "sketchPlane" : qUnion([Q0])});
            skLineSegment(sketch, "E152.bottom", {"start": v(-69.84, 46.03) * mm, "end": v(-36.4, 46.03) * mm});
            skLineSegment(sketch, "E152.top", {"start": v(-65.84, 35) * mm, "end": v(-40.4, 35) * mm});
            skLineSegment(sketch, "E152.left", {"start": v(-69.84, 46.03) * mm, "end": v(-69.84, 39) * mm});
            skLineSegment(sketch, "E152.right", {"start": v(-36.4, 46.03) * mm, "end": v(-36.4, 39) * mm});
            skPoint(sketch, "E153.visualSharp", {"position": v(-36.4, 35) * mm});
            skArc(sketch, "E153.filletArc", {"start": v(-40.4, 35) * mm, "mid": v(-37.58, 36.18) * mm, "end": v(-36.4, 39) * mm});
            skPoint(sketch, "E154.visualSharp", {"position": v(-69.84, 35) * mm});
            skArc(sketch, "E154.filletArc", {"start": v(-69.84, 39) * mm, "mid": v(-68.67, 36.18) * mm, "end": v(-65.84, 35) * mm});
            skText(sketch, "E155", { "text": "BULU", "fontName": "OpenSans-Bold.ttf"});
            const initialGuessF6  = {"E155": [-0.06691, 0.0372, 1, 0, 0.00749]};
            skSetInitialGuess(sketch, initialGuessF6);
            skSolve(sketch);
        }
        {
            var Q0;
            Q0=makeQuery(id+"F6.imprint","IMPRINT",FACE,{"disambiguationData":[TD([[makeQuery(id+"F6.imprint","IMPRINT",EDGE,{"derivedFrom":sQuery(id+"F6.wireOp",EDGE,"E152.bottom")}),-1.0]])]});
            var Q1;
            Q1=makeQuery(id+"F5.boolean.opBoolean","MERGE",FACE,{"derivedFrom":[makeQuery(id+"F3.opExtrude","CAP_FACE",FACE,{"disambiguationData":[OSD([sQuery(id+"F1.wireOp",EDGE,"E91.bottom"),sQuery(id+"F1.wireOp",EDGE,"E91.top"),sQuery(id+"F1.wireOp",EDGE,"E91.left"),sQuery(id+"F1.wireOp",EDGE,"E91.right"),sQuery(id+"F1.wireOp",EDGE,"E92.filletArc"),sQuery(id+"F1.wireOp",EDGE,"E93.filletArc"),sQuery(id+"F1.wireOp",EDGE,"E94.filletArc"),sQuery(id+"F1.wireOp",EDGE,"E95.filletArc"),sQuery(id+"F1.wireOp",EDGE,"E100.bottom"),sQuery(id+"F1.wireOp",EDGE,"E107.0"),sQuery(id+"F1.wireOp",EDGE,"E107.1"),sQuery(id+"F1.wireOp",EDGE,"E107.2"),sQuery(id+"F1.wireOp",EDGE,"E107.3"),sQuery(id+"F1.wireOp",EDGE,"E107.4"),sQuery(id+"F1.wireOp",EDGE,"E107.5"),sQuery(id+"F1.wireOp",EDGE,"E107.6"),sQuery(id+"F1.wireOp",EDGE,"E107.7")])],"isStart":false}),makeQuery(id+"F5.opExtrude","CAP_FACE",FACE,{"disambiguationData":[OSD([sQuery(id+"F4.wireOp",EDGE,"E121.0.startCap"),sQuery(id+"F4.wireOp",EDGE,"E121.0.endCap"),sQuery(id+"F4.wireOp",EDGE,"E121.0.left"),sQuery(id+"F4.wireOp",EDGE,"E121.0.right")])],"isStart":false}),makeQuery(id+"F5.opExtrude","CAP_FACE",FACE,{"disambiguationData":[OSD([sQuery(id+"F4.wireOp",EDGE,"E127.0.startCap"),sQuery(id+"F4.wireOp",EDGE,"E127.0.endCap"),sQuery(id+"F4.wireOp",EDGE,"E127.0.left"),sQuery(id+"F4.wireOp",EDGE,"E127.0.right")])],"isStart":false}),makeQuery(id+"F5.opExtrude","CAP_FACE",FACE,{"disambiguationData":[OSD([sQuery(id+"F4.wireOp",EDGE,"E138.0.left"),sQuery(id+"F4.wireOp",EDGE,"E138.0.right"),sQuery(id+"F4.wireOp",EDGE,"E138.0.endCap"),sQuery(id+"F4.wireOp",EDGE,"E138.0.startCap")])],"isStart":false}),makeQuery(id+"F5.opExtrude","CAP_FACE",FACE,{"disambiguationData":[OSD([sQuery(id+"F4.wireOp",EDGE,"E142.0.endCap"),sQuery(id+"F4.wireOp",EDGE,"E142.0.left"),sQuery(id+"F4.wireOp",EDGE,"E142.0.startCap"),sQuery(id+"F4.wireOp",EDGE,"E142.0.right")])],"isStart":false}),makeQuery(id+"F5.opExtrude","CAP_FACE",FACE,{"disambiguationData":[OSD([sQuery(id+"F4.wireOp",EDGE,"E146.0.left"),sQuery(id+"F4.wireOp",EDGE,"E146.0.right"),sQuery(id+"F4.wireOp",EDGE,"E146.0.startCap"),sQuery(id+"F4.wireOp",EDGE,"E146.0.endCap")])],"isStart":false}),makeQuery(id+"F5.opExtrude","CAP_FACE",FACE,{"disambiguationData":[OSD([sQuery(id+"F4.wireOp",EDGE,"E148.0.left"),sQuery(id+"F4.wireOp",EDGE,"E148.0.right"),sQuery(id+"F4.wireOp",EDGE,"E148.0.startCap"),sQuery(id+"F4.wireOp",EDGE,"E148.0.endCap")])],"isStart":false}),makeQuery(id+"F5.opExtrude","CAP_FACE",FACE,{"disambiguationData":[OSD([sQuery(id+"F4.wireOp",EDGE,"E150.0.left"),sQuery(id+"F4.wireOp",EDGE,"E150.0.right"),sQuery(id+"F4.wireOp",EDGE,"E150.0.startCap"),sQuery(id+"F4.wireOp",EDGE,"E150.0.endCap")])],"isStart":false})]});
            extrude(context, id + "F7", {"entities" : qUnion([Q0]), "operationType" : NewBodyOperationType.ADD, "endBound" : BoundingType.UP_TO_SURFACE, "endBoundEntityFace" : qUnion([Q1]), "depth" : 25 * mm});
        }
    });
